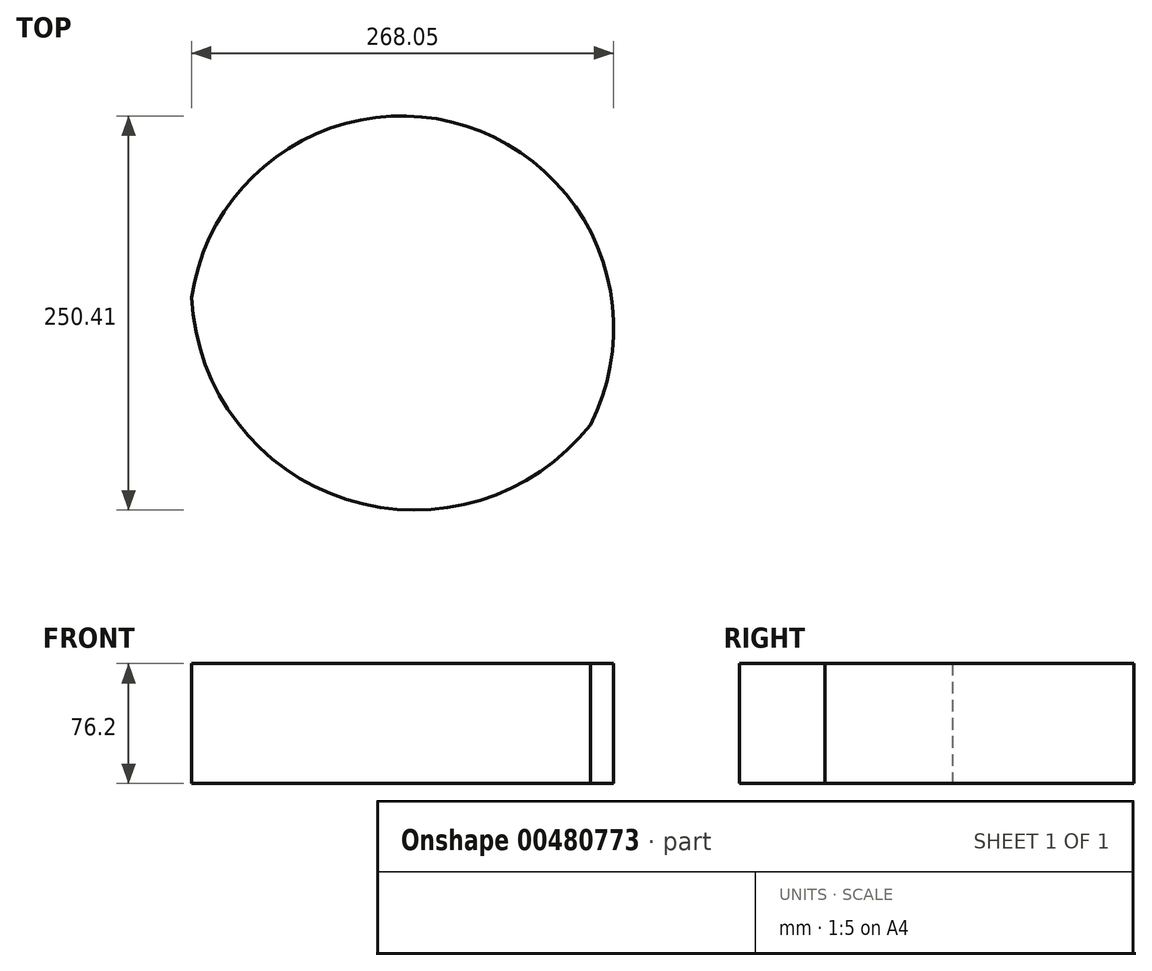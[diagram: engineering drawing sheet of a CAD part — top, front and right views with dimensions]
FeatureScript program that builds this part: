
annotation { "Feature Type Name" : "Feature", "Feature Type Description" : "" }
export const myFeature = defineFeature(function(context is Context, id is Id, definition is map)
    precondition{}
    {
        {
            var Q0;
            Q0=qCreatedBy(makeId("Top.planeOp"),FACE);
            var sketch = newSketch(context, id + "F0", { "sketchPlane" : qUnion([Q0])});
            skCircle(sketch, "E0", {"center": v(66.47, -42.7) * mm, "radius": 141.84 * mm});
            skCircle(sketch, "E1", {"center": v(58.1, -68.86) * mm, "radius": 134.73 * mm});
            skSolve(sketch);
        }
        {
            var Q0;
            {var subQ0=sQuery(id+"F0.wireOp",EDGE,"E1");var subQ1=sQuery(id+"F0.wireOp",EDGE,"E0");var subQ2=makeQuery(id+"F0.imprint","INTERSECT",VERTEX,{"disambiguationData":[OD(0.0)],"derivedFrom":[subQ1,subQ0]});Q0=makeQuery(id+"F0.imprint","IMPRINT",FACE,{"disambiguationData":[TD([[makeQuery(id+"F0.imprint","IMPRINT",EDGE,{"disambiguationData":[TD([[subQ2,-1.0]])],"derivedFrom":subQ1}),1.0]])]});}
            extrude(context, id + "F1", {"entities" : qUnion([Q0]), "depth" : 76.2 * mm});
        }
    });
